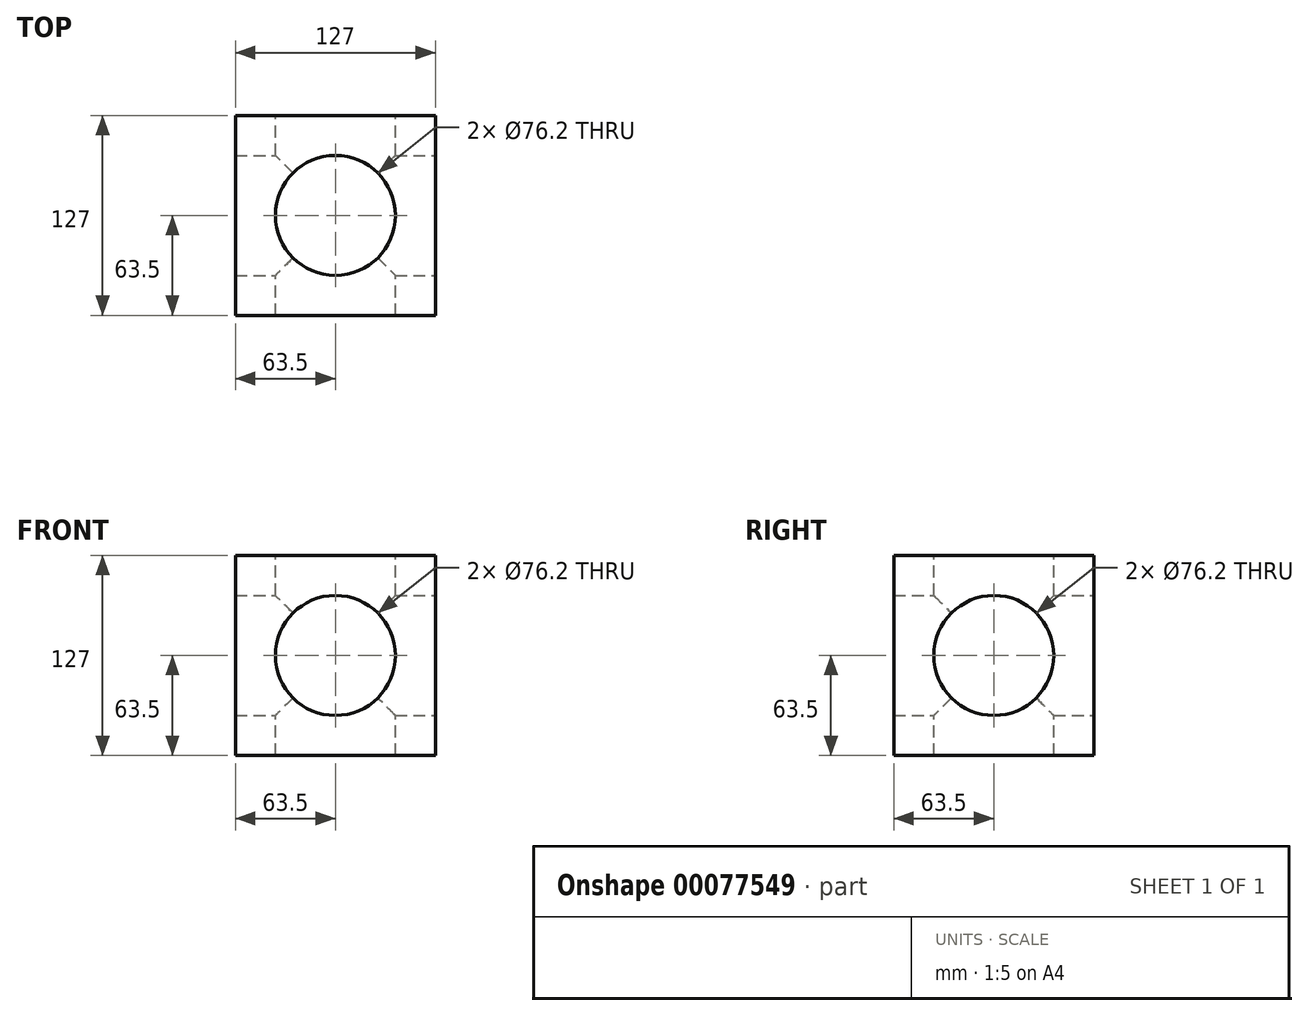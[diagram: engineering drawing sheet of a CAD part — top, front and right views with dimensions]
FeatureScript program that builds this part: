
annotation { "Feature Type Name" : "Feature", "Feature Type Description" : "" }
export const myFeature = defineFeature(function(context is Context, id is Id, definition is map)
    precondition{}
    {
        {
            var Q0;
            Q0=qCreatedBy(makeId("Top.planeOp"),FACE);
            var sketch = newSketch(context, id + "F0", { "sketchPlane" : qUnion([Q0])});
            skLineSegment(sketch, "E0.bottom", {"start": v(-63.5, 63.5) * mm, "end": v(63.5, 63.5) * mm});
            skLineSegment(sketch, "E0.top", {"start": v(-63.5, -63.5) * mm, "end": v(63.5, -63.5) * mm});
            skLineSegment(sketch, "E0.left", {"start": v(-63.5, 63.5) * mm, "end": v(-63.5, -63.5) * mm});
            skLineSegment(sketch, "E0.right", {"start": v(63.5, 63.5) * mm, "end": v(63.5, -63.5) * mm});
            skSolve(sketch);
        }
        {
            var Q0;
            Q0=makeQuery(id+"F0.imprint","IMPRINT",FACE,{"disambiguationData":[TD([[makeQuery(id+"F0.imprint","IMPRINT",EDGE,{"derivedFrom":sQuery(id+"F0.wireOp",EDGE,"E0.bottom")}),-1.0]])]});
            extrude(context, id + "F1", {"entities" : qUnion([Q0]), "depth" : 127 * mm});
        }
        {
            var Q0;
            Q0=makeQuery(id+"F1.opExtrude","SWEPT_FACE",FACE,{"disambiguationData":[OSD([sQuery(id+"F0.wireOp",EDGE,"E0.bottom")])]});
            var sketch = newSketch(context, id + "F2", { "sketchPlane" : qUnion([Q0])});
            skLineSegment(sketch, "E1", {"start": v(-63.5, 127) * mm, "end": v(63.5, 0) * mm, "construction": true});
            skLineSegment(sketch, "E2", {"start": v(63.5, 127) * mm, "end": v(-63.5, 0) * mm, "construction": true});
            skCircle(sketch, "E3", {"center": v(0, 63.5) * mm, "radius": 38.1 * mm});
            skSolve(sketch);
        }
        {
            var Q0;
            Q0=makeQuery(id+"F2.imprint","IMPRINT",FACE,{"disambiguationData":[TD([[makeQuery(id+"F2.imprint","IMPRINT",EDGE,{"derivedFrom":sQuery(id+"F2.wireOp",EDGE,"E3")}),1.0]])]});
            extrude(context, id + "F3", {"entities" : qUnion([Q0]), "operationType" : NewBodyOperationType.REMOVE, "oppositeDirection" : true, "depth" : 127 * mm});
        }
        {
            var Q0;
            Q0=makeQuery(id+"F1.opExtrude","SWEPT_FACE",FACE,{"disambiguationData":[OSD([sQuery(id+"F0.wireOp",EDGE,"E0.right")])]});
            var sketch = newSketch(context, id + "F4", { "sketchPlane" : qUnion([Q0])});
            skLineSegment(sketch, "E4", {"start": v(-63.5, 127) * mm, "end": v(63.5, 0) * mm, "construction": true});
            skLineSegment(sketch, "E5", {"start": v(-63.5, 0) * mm, "end": v(63.5, 127) * mm, "construction": true});
            skCircle(sketch, "E6", {"center": v(0, 63.5) * mm, "radius": 38.1 * mm});
            skSolve(sketch);
        }
        {
            var Q0;
            Q0=makeQuery(id+"F4.imprint","IMPRINT",FACE,{"disambiguationData":[TD([[makeQuery(id+"F4.imprint","IMPRINT",EDGE,{"derivedFrom":sQuery(id+"F4.wireOp",EDGE,"E6")}),1.0]])]});
            extrude(context, id + "F5", {"entities" : qUnion([Q0]), "operationType" : NewBodyOperationType.REMOVE, "oppositeDirection" : true, "depth" : 127 * mm});
        }
        {
            var Q0;
            Q0=makeQuery(id+"F1.opExtrude","CAP_FACE",FACE,{"disambiguationData":[OSD([sQuery(id+"F0.wireOp",EDGE,"E0.bottom"),sQuery(id+"F0.wireOp",EDGE,"E0.top"),sQuery(id+"F0.wireOp",EDGE,"E0.left"),sQuery(id+"F0.wireOp",EDGE,"E0.right")])],"isStart":false});
            var sketch = newSketch(context, id + "F6", { "sketchPlane" : qUnion([Q0])});
            skLineSegment(sketch, "E7", {"start": v(-63.5, -63.5) * mm, "end": v(63.5, 63.5) * mm, "construction": true});
            skLineSegment(sketch, "E8", {"start": v(63.5, -63.5) * mm, "end": v(-63.5, 63.5) * mm, "construction": true});
            skCircle(sketch, "E9", {"center": v(0, 0) * mm, "radius": 38.1 * mm});
            skSolve(sketch);
        }
        {
            var Q0;
            Q0=makeQuery(id+"F6.imprint","IMPRINT",FACE,{"disambiguationData":[TD([[makeQuery(id+"F6.imprint","IMPRINT",EDGE,{"derivedFrom":sQuery(id+"F6.wireOp",EDGE,"E9")}),1.0]])]});
            extrude(context, id + "F7", {"entities" : qUnion([Q0]), "operationType" : NewBodyOperationType.REMOVE, "oppositeDirection" : true, "depth" : 127 * mm});
        }
    });
